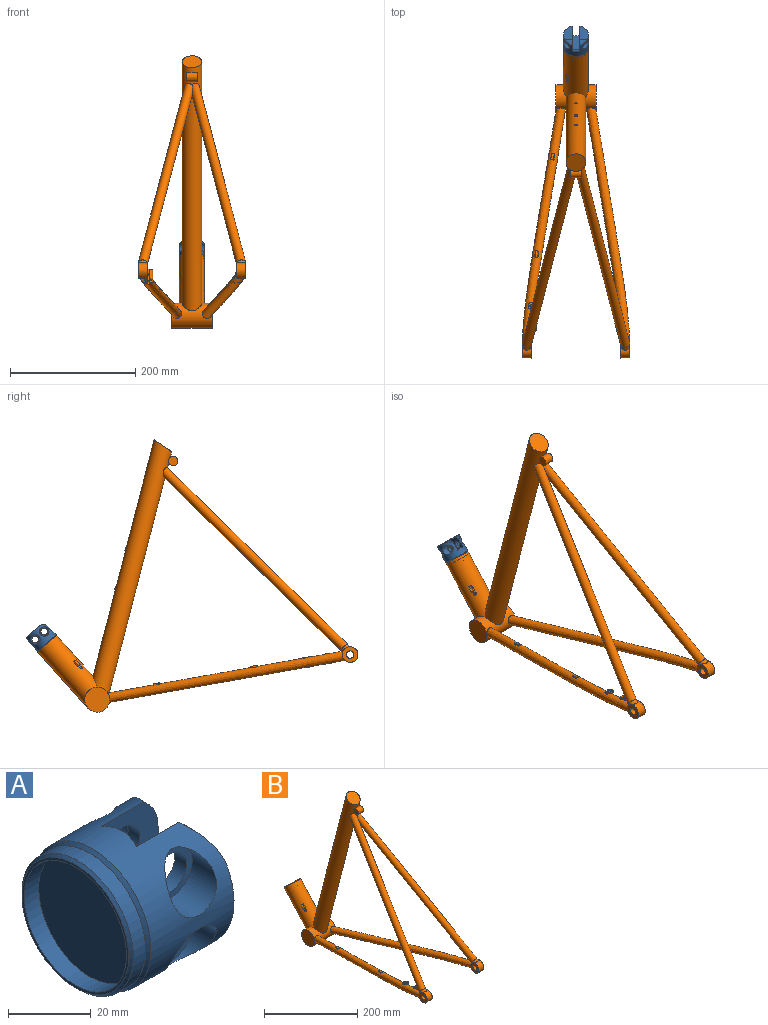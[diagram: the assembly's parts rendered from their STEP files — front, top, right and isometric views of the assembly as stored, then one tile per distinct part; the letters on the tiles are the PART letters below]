
ASSEMBLY  parts=2 mates=3
PART A: 28 faces, bbox 34.3x40x40 mm
  f0: cylinder r=12.2mm len=12mm, axis (0,1,0), area 145mm2, adj f1,f4,f9,f21
  f1: plane 29.5x12mm, normal (1,0,0), area 350.3mm2, adj f0,f4,f9,f21
  f2: cylinder r=7.5mm len=15mm, axis (0,-1,0), area 304.4mm2, adj f9,f16
  f3: cylinder r=7.5mm len=15mm, axis (0,-1,0), area 304.1mm2, adj f9,f15
  f4: plane 38.16x24mm, normal (0,-1,0), area 694.7mm2, adj f0,f1,f5,f6,f7,f8,f9
  f5: cylinder r=5.55mm len=11.1mm, axis (0,-1,0), area 139.5mm2, adj f4,f16
  f6: cylinder r=11.8mm len=11.6mm, axis (0,-1,0), area 76.8mm2, adj f4,f8,f9
  f7: cylinder r=5.55mm len=11.1mm, axis (0,-1,0), area 139.5mm2, adj f4,f15
  f8: plane 28.58x14mm, normal (1,0,0), area 321.6mm2, adj f4,f6,f9
  f9: cylinder r=20mm len=40mm, axis (-1,0,0), area 2147.3mm2, adj f0,f1,f2,f3,f4,f6,f8,f17
  f10: plane 38.2x38.2mm, normal (-1,0,0), area 6mm2, adj f12,f17
  f11: cylinder r=17.5mm len=35mm, axis (1,0,0), area 549.8mm2, adj f13,f14
  f12: cylinder r=19.05mm len=38.1mm, axis (1,0,0), area 502.7mm2, adj f10,f18
  f13: plane 36.5x36.5mm, normal (-1,0,0), area 84.2mm2, adj f11,f18
  f14: plane 35x35mm, normal (-1,0,0), area 962.1mm2, adj f11
  f15: plane 15x15mm, normal (0,1,0), area 79.9mm2, adj f3,f7
  f16: plane 15x15mm, normal (0,1,0), area 79.9mm2, adj f2,f5
  f17: cone r=20mm half-angle=45deg, axis (1,0,0), area 156.3mm2, adj f9,f10
  f18: cone r=18.25mm half-angle=45deg, axis (1,0,0), area 132.6mm2, adj f12,f13
  f19: cylinder r=7.5mm len=15mm, axis (0,1,0), area 304.2mm2, adj f9,f27
  f20: cylinder r=7.5mm len=15mm, axis (0,1,0), area 304.4mm2, adj f9,f26
  f21: plane 38.16x24mm, normal (0,1,0), area 694.7mm2, adj f0,f1,f9,f22,f23,f24,f25
  f22: cylinder r=5.55mm len=11.1mm, axis (0,1,0), area 139.5mm2, adj f21,f27
  f23: cylinder r=11.8mm len=11.6mm, axis (0,1,0), area 76.8mm2, adj f9,f21,f25
  f24: cylinder r=5.55mm len=11.1mm, axis (0,1,0), area 139.5mm2, adj f21,f26
  f25: plane 28.58x14mm, normal (1,0,0), area 321.6mm2, adj f9,f21,f23
  f26: plane 15x15mm, normal (0,-1,0), area 79.9mm2, adj f20,f24
  f27: plane 15x15mm, normal (0,-1,0), area 79.9mm2, adj f19,f22
PART B: 96 faces, bbox 174.9x514x438 mm
  f0: bspline ~382.62x82.41mm, area 18053.9mm2, adj f1,f69,f70,f72,f73,f74,f75
  f1: cylinder r=7.5mm len=15.84mm, axis (0,0.71,0.7), area 188.7mm2, adj f0,f2,f69,f73
  f2: cylinder r=7.5mm len=299.06mm, axis (-0.18,0.7,0.69), area 19019.4mm2, adj f1,f3,f27
  f3: cylinder r=15.9mm len=407.25mm, axis (0,0.25,-0.97), area 39169.3mm2, adj f2,f4,f6,f10,f13,f17,f26,f27
  f4: cylinder r=2mm len=16.4mm, axis (0,-0.97,-0.25), area 199.8mm2, adj f3,f5
  f5: plane 4x3.87mm, normal (0,0.97,0.25), area 12.6mm2, adj f4
  f6: cylinder r=3mm len=6.08mm, axis (0,-0.97,-0.25), area 20.7mm2, adj f3,f7
  f7: plane 6x5.81mm, normal (0,0.97,0.25), area 15.7mm2, adj f6,f8
  f8: cylinder r=2mm len=4.15mm, axis (0,-0.97,-0.25), area 13.8mm2, adj f7,f9
  f9: cylinder r=15.9mm len=4mm, axis (0,0.25,-0.97), area 12.6mm2, adj f8
  f10: cylinder r=7.5mm len=16mm, axis (-1,0,0), area 665.4mm2, adj f3,f11,f12
  f11: plane 15x15mm, normal (1,0,0), area 176.7mm2, adj f10
  f12: plane 15x15mm, normal (-1,0,0), area 176.7mm2, adj f10
  f13: cylinder r=3mm len=6.08mm, axis (0,-0.97,-0.25), area 20.7mm2, adj f3,f14
  f14: plane 6x5.81mm, normal (0,0.97,0.25), area 15.7mm2, adj f13,f15
  f15: cylinder r=2mm len=4.15mm, axis (0,-0.97,-0.25), area 13.8mm2, adj f14,f16
  f16: cylinder r=15.9mm len=4mm, axis (0,0.25,-0.97), area 12.6mm2, adj f15
  f17: cylinder r=20mm len=116.13mm, axis (0,-0.67,-0.75), area 12766.5mm2, adj f3,f18,f20,f22,f23,f24,f25,f75
  f18: cylinder r=2mm len=15.01mm, axis (0,0.75,-0.67), area 187mm2, adj f17,f19
  f19: plane 4x2.98mm, normal (0,-0.75,0.67), area 12.6mm2, adj f18
  f20: plane 8.09x7.37mm, normal (0.35,-0.7,0.63), area 27.3mm2, adj f17,f21,f22,f24
  f21: cylinder r=2.5mm len=9.4mm, axis (0,0.67,0.75), area 45.7mm2, adj f20,f22,f23,f24
  f22: plane 5.25x3.76mm, normal (0,0.67,0.75), area 8.1mm2, adj f17,f20,f21,f23
  f23: plane 8.88x8.26mm, normal (-0.9,0.33,-0.29), area 23.8mm2, adj f17,f21,f22,f24
  f24: plane 5.25x3.76mm, normal (0,-0.67,-0.75), area 8.1mm2, adj f17,f20,f21,f23
  f25: plane 40x29.82mm, normal (0,0.67,0.75), area 1256.6mm2, adj f17
  f26: plane 34.75x30.83mm, normal (0,-0.57,0.82), area 845.2mm2, adj f3
  f27: cylinder r=7.5mm len=299.05mm, axis (0.18,0.7,0.69), area 19019.5mm2, adj f2,f3,f28
  f28: cylinder r=7.5mm len=15.84mm, axis (0,0.71,0.7), area 188.7mm2, adj f27,f29,f67,f68
  f29: bspline ~382.62x82.41mm, area 17440.6mm2, adj f28,f30,f32,f33,f34,f35,f37,f38
  f30: plane 10.16x4.19mm, normal (-0.98,0.18,0.13), area 24.4mm2, adj f29,f31,f32,f34
  f31: cylinder r=2.5mm len=10.43mm, axis (-0.16,-0.97,0.17), area 52.3mm2, adj f30,f32,f33,f34
  f32: plane 5.68x2.85mm, normal (0.16,0.97,-0.17), area 5mm2, adj f29,f30,f31,f33
  f33: plane 10.25x3.75mm, normal (0.94,-0.09,0.33), area 20.9mm2, adj f29,f31,f32,f34
  f34: plane 5.68x2.85mm, normal (-0.16,-0.97,0.17), area 5mm2, adj f29,f30,f31,f33
  f35: plane 10.2x4.21mm, normal (-0.98,0.18,0.13), area 24.2mm2, adj f29,f36,f37,f39
  f36: cylinder r=2.5mm len=10.43mm, axis (-0.16,-0.97,0.17), area 52.3mm2, adj f35,f37,f38,f39
  f37: plane 5.66x2.8mm, normal (0.16,0.97,-0.17), area 5mm2, adj f29,f35,f36,f38
  f38: plane 10.29x3.81mm, normal (0.94,-0.09,0.33), area 21mm2, adj f29,f36,f37,f39
  f39: plane 5.68x2.84mm, normal (-0.16,-0.97,0.17), area 5mm2, adj f29,f35,f36,f38
  f40: plane 16.08x3.33mm, normal (0,0.98,-0.18), area 34.6mm2, adj f29,f41,f46,f47,f48,f50
  f41: plane 14.02x10.85mm, normal (0,-0.18,-0.98), area 93.6mm2, adj f40,f42,f43,f44,f45,f46,f48,f49
  f42: cylinder r=2.51mm len=16.63mm, axis (0,0.18,0.98), area 126.2mm2, adj f41,f43,f45,f47
  f43: plane 15.75x3mm, normal (0,0.98,-0.18), area 48mm2, adj f41,f42,f44,f47
  f44: cylinder r=2.51mm len=16.63mm, axis (0,0.18,0.98), area 126.2mm2, adj f41,f43,f45,f47
  f45: plane 15.75x3mm, normal (0,-0.98,0.18), area 48mm2, adj f41,f42,f44,f47
  f46: cylinder r=5.51mm len=17.69mm, axis (0,0.18,0.98), area 277mm2, adj f40,f41,f47,f49
  f47: plane 14.02x10.85mm, normal (0,0.18,0.98), area 93.6mm2, adj f40,f42,f43,f44,f45,f46,f49,f50
  f48: cylinder r=5.51mm len=11.57mm, axis (0,0.18,0.98), area 20.5mm2, adj f29,f40,f41,f49
  f49: plane 15.9x3.15mm, normal (0,-0.98,0.18), area 42.1mm2, adj f29,f41,f46,f47,f48,f50
  f50: cylinder r=5.51mm len=11.57mm, axis (0,0.18,0.98), area 20.5mm2, adj f29,f40,f47,f49
  f51: cylinder r=6mm len=15mm, axis (-1,0,0), area 565.5mm2, adj f29,f52,f66
  f52: plane 25x25mm, normal (-1,0,0), area 377.8mm2, adj f51,f68
  f53: plane 4.16x3.26mm, normal (0,-0.98,0.18), area 7.1mm2, adj f29,f54,f63,f65
  f54: plane 14.02x10.85mm, normal (0,-0.18,-0.98), area 93.6mm2, adj f53,f55,f57,f58,f59,f63,f64,f65
  f55: cylinder r=2.51mm len=16.63mm, axis (0,0.18,0.98), area 126.2mm2, adj f54,f56,f57,f59
  f56: plane 14.02x10.85mm, normal (0,0.18,0.98), area 93.6mm2, adj f55,f57,f58,f59,f60,f61,f62,f63
  f57: plane 15.75x3mm, normal (0,0.98,-0.18), area 48mm2, adj f54,f55,f56,f58
  f58: cylinder r=2.51mm len=16.63mm, axis (0,0.18,0.98), area 126.2mm2, adj f54,f56,f57,f59
  f59: plane 15.75x3mm, normal (0,-0.98,0.18), area 48mm2, adj f54,f55,f56,f58
  f60: plane 4.14x3.23mm, normal (0,-0.98,0.18), area 7.1mm2, adj f29,f56,f61,f63
  f61: cylinder r=5.51mm len=11.07mm, axis (0,0.18,0.98), area 12.9mm2, adj f29,f56,f60,f62
  f62: plane 3.22x2.65mm, normal (0,0.98,-0.18), area 4.4mm2, adj f29,f56,f61,f63
  f63: cylinder r=5.51mm len=17.69mm, axis (0,0.18,0.98), area 251.6mm2, adj f29,f53,f54,f56,f60,f62,f64
  f64: plane 3.24x2.68mm, normal (0,0.98,-0.18), area 4.4mm2, adj f29,f54,f63,f65
  f65: cylinder r=5.51mm len=11.07mm, axis (0,0.18,0.98), area 13.5mm2, adj f29,f53,f54,f64
  f66: plane 25.13x25.13mm, normal (1,0,0), area 363.7mm2, adj f29,f51,f67,f68
  f67: cylinder r=12.5mm len=10.44mm, axis (1,0,0), area 22.3mm2, adj f28,f29,f66
  f68: cylinder r=12.5mm len=25mm, axis (1,0,0), area 816.8mm2, adj f28,f29,f52,f66
  f69: cylinder r=12.5mm len=10.44mm, axis (-1,0,0), area 22.3mm2, adj f0,f1,f72
  f70: cylinder r=6mm len=15mm, axis (1,0,0), area 565.5mm2, adj f0,f71,f72
  f71: plane 25x25mm, normal (1,0,0), area 377.8mm2, adj f70,f73
  f72: plane 25.13x25.13mm, normal (-1,0,0), area 363.7mm2, adj f0,f69,f70,f73
  f73: cylinder r=12.5mm len=25mm, axis (-1,0,0), area 817mm2, adj f0,f1,f71,f72
  f74: cylinder r=2mm len=4.29mm, axis (0,0.18,0.98), area 25.1mm2, adj f0
  f75: cylinder r=20mm len=64mm, axis (-1,0,0), area 5756.2mm2, adj f0,f3,f17,f29,f76,f77
  f76: plane 40x40mm, normal (1,0,0), area 1256.6mm2, adj f75
  f77: plane 40x40mm, normal (-1,0,0), area 1256.6mm2, adj f75
  f78: cylinder r=12.5mm len=11.01mm, axis (-1,0,0), area 97.6mm2
  f79: cylinder r=20mm len=11.14mm, axis (-1,0,0), area 97.2mm2
  f80: cylinder r=5.51mm len=4.21mm, axis (0,0.18,0.98), area 1.2mm2, adj f81
  f81: plane 10.02x3mm, normal (0,-0.98,0.18), area 24mm2, adj f80,f82
  f82: cylinder r=5.51mm len=12.71mm, axis (0,0.18,0.98), area 174.7mm2, adj f81,f83
  f83: plane 8.6x2.18mm, normal (0,0.98,-0.18), area 13.3mm2, adj f82
  f84: plane 2.98x0.47mm, normal (0.16,0.97,-0.17), area 0.4mm2, adj f85
  f85: plane 10.2x4.52mm, normal (0,0.18,0.98), area 30.2mm2, adj f84,f86
  f86: plane 2.98x0.47mm, normal (-0.16,-0.97,0.17), area 0.4mm2, adj f85
  f87: plane 2.98x0.47mm, normal (0.16,0.97,-0.17), area 0.4mm2, adj f88
  f88: plane 10.19x4.57mm, normal (0,0.18,0.98), area 30.2mm2, adj f87,f89
  f89: plane 2.98x0.47mm, normal (-0.16,-0.97,0.17), area 0.4mm2, adj f88
  f90: cylinder r=12.5mm len=11.01mm, axis (1,0,0), area 97.6mm2
  f91: cylinder r=20mm len=11.14mm, axis (-1,0,0), area 97.1mm2
  f92: cylinder r=5.51mm len=12.71mm, axis (0,0.18,0.98), area 151.3mm2
  f93: cylinder r=3.53mm len=7.05mm, axis (1,0,0), area 110.8mm2, adj f94,f95
  f94: plane 7.05x7.05mm, normal (-1,0,0), area 39.1mm2, adj f93
  f95: plane 7.05x7.05mm, normal (1,0,0), area 39.1mm2, adj f93
PLACE A rot(axis=(0.38,-0.38,0.85),99.6deg) t=(-262.45,284.25,60.61)mm
PLACE B t=(-262.45,189.37,-15.54)mm
MATE cylindrical A.f9 <-> B.f17  axis (0,0.67,0.75) through (-262.45,267.93,72.37)mm
MATE planar B.f17 <-> A.f9  axis (0,0.67,0.75) through (-262.45,269.33,73.93)mm
MATE parallel A.f4 <-> B.f75  axis (1,0,0) through (-268.45,281.32,86.34)mm
